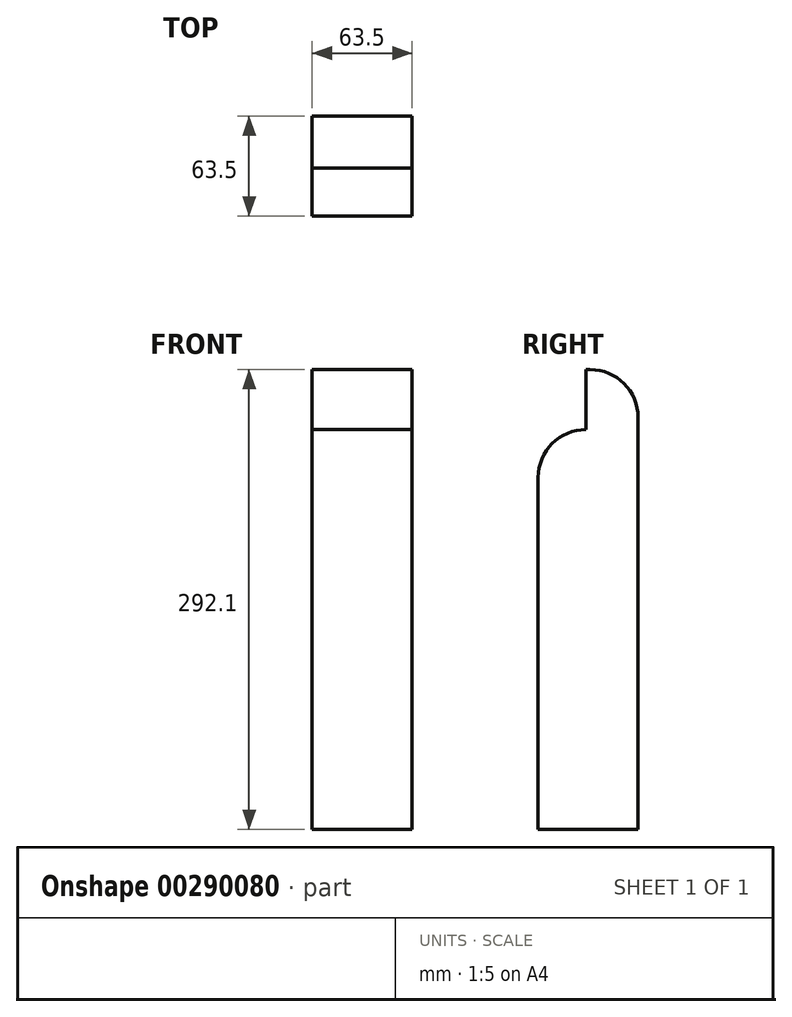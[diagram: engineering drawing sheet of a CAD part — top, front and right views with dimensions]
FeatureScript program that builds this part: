
annotation { "Feature Type Name" : "Feature", "Feature Type Description" : "" }
export const myFeature = defineFeature(function(context is Context, id is Id, definition is map)
    precondition{}
    {
        {
            var Q0;
            Q0=qCreatedBy(makeId("Top.planeOp"),FACE);
            var sketch = newSketch(context, id + "F0", { "sketchPlane" : qUnion([Q0])});
            skLineSegment(sketch, "E0.bottom", {"start": v(0, 0) * mm, "end": v(63.5, 0) * mm});
            skLineSegment(sketch, "E0.top", {"start": v(0, 63.5) * mm, "end": v(63.5, 63.5) * mm});
            skLineSegment(sketch, "E0.left", {"start": v(0, 0) * mm, "end": v(0, 63.5) * mm});
            skLineSegment(sketch, "E0.right", {"start": v(63.5, 0) * mm, "end": v(63.5, 63.5) * mm});
            skSolve(sketch);
        }
        {
            var Q0;
            Q0 = qSketchRegion(id + "F0", true);
            extrude(context, id + "F1", {"entities" : qUnion([Q0]), "depth" : 254 * mm});
        }
        {
            var Q0;
            Q0=makeQuery(id+"F1.opExtrude","CAP_EDGE",EDGE,{"disambiguationData":[OSD([sQuery(id+"F0.wireOp",EDGE,"E0.bottom")])],"isStart":false});
            fillet(context, id + "F2", {"entities" : qUnion([Q0]), "radius" : 30.48 * mm, "tangentPropagation" : true, "allowEdgeOverflow" : false});
        }
        {
            var Q0;
            Q0=makeQuery(id+"F1.opExtrude","CAP_FACE",FACE,{"disambiguationData":[OSD([sQuery(id+"F0.wireOp",EDGE,"E0.bottom"),sQuery(id+"F0.wireOp",EDGE,"E0.top"),sQuery(id+"F0.wireOp",EDGE,"E0.left"),sQuery(id+"F0.wireOp",EDGE,"E0.right")])],"isStart":false});
            var sketch = newSketch(context, id + "F3", { "sketchPlane" : qUnion([Q0])});
            skLineSegment(sketch, "E1.bottom", {"start": v(0, 30.48) * mm, "end": v(63.5, 30.48) * mm});
            skLineSegment(sketch, "E1.top", {"start": v(0, 63.5) * mm, "end": v(63.5, 63.5) * mm});
            skLineSegment(sketch, "E1.left", {"start": v(0, 30.48) * mm, "end": v(0, 63.5) * mm});
            skLineSegment(sketch, "E1.right", {"start": v(63.5, 30.48) * mm, "end": v(63.5, 63.5) * mm});
            skSolve(sketch);
        }
        {
            var Q0;
            Q0 = qSketchRegion(id + "F3", true);
            extrude(context, id + "F4", {"entities" : qUnion([Q0]), "operationType" : NewBodyOperationType.ADD, "depth" : 38.1 * mm});
        }
        {
            var Q0;
            Q0=makeQuery(id+"F4.opExtrude","CAP_EDGE",EDGE,{"disambiguationData":[OSD([sQuery(id+"F3.wireOp",EDGE,"E1.top")])],"isStart":false});
            fillet(context, id + "F5", {"entities" : qUnion([Q0]), "radius" : 30.48 * mm, "tangentPropagation" : true, "allowEdgeOverflow" : false});
        }
    });
